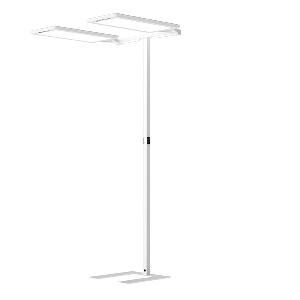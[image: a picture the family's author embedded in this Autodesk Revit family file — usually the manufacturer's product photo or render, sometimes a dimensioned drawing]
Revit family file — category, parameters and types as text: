
# Revit family: yara_doubleu_-_yus_2_15000_vtl_r_ws_cee_s0_c_114268000-00812019_adc4
name_source: partatom
category: Lighting Fixtures
units: mm (PartAtom-declared; Revit-internal decimal feet)

## family parameters
Cut with Voids When Loaded = No
Host = Face
Light Source = No
Part Type = Normal
Room Calculation Point = No
Round Connector Dimension = Use Diameter
Shared = No

## types (1)
- YARA.doubleU - YUS 2/15000/VTL/R/WS/CEE/S0/C (1 x LED, 15000 lm, VTL)
    Apparent Load = 214 VA
    Approval mark = CE
    CIE Flux Codes = 58 87 97 13 100
    Color Rendering = 80-89
    Color Temperature = VTL
    Control Gear = Electronic ballast
    Default Elevation = 1800 mm
    Description = YUS 2/15000/VTL/R/WS/CEE/S0/C|Free-standing luminaire|light source: LED Cold white   |work equipment: Electronic ballast DALI|connected load: 220-240V, 50/60Hz|Power consumption: approx. 210 W|power factor: approx. 0,966|luminous flux: 30000 lm|luminous efficacy: 142 lm/W|light distribution: Direct/indirect|direct ratio: approx. 13 %|color rendering index (CRI): >= 80|chromaticity tolerance:  3 SDCM|technology: Presence and daylight sensor control (PIR)|operation: Wireless switch|luminaire body|material: Aluminium/plastic|surface: Powder coatet|colour: White|lamp cover: Acrylic (PMMA)|tubular section|material: Steel tube|surface: Powder-coated|Form: Tubular section upright|colour of tubular section: White|luminaire base|Form: C-form flat|weight (net): approx. 26.0 kg|mains lead: 3.00 m Mains plug CEE 7/VII|Fastening: Floor standing base|glare control: Conical prismatic screen|luminance(L65): <= 2700 cd/m|unified glare rating(4H 8H): <=  16|special features: App control, Asymmetric radiation, Biodynamic light VTL, Direct and indirect lighting component with edge light and light guidetechnology for a homogeneous light exit, Flicker-free, Magnetic control panel, freely positionable, PIR movement and daylight sensor, TALK Bluetooth|Approval mark: VDE - ENEC|
    Frequency = 50 Hz, 60 Hz
    Height = 24 mm  [stored 0.0787402 ft]
    Lamp = 1 x LED
    Lamp Light Flux = 15000 lm
    Lamp count = 1
    Length = 690 mm
    Luminous efficacy = 140 lm/W
    Manufacturer = Waldmann
    ModVariant = No
    Model = 114268000-00812019
    Mounting Place = Floor
    Mounting Type = Freestanding
    Number of Poles = 1
    OnlyDefault = Yes
    Power Factor = 1
    Product Name = YARA.doubleU - YUS 2/15000/VTL/R/WS/CEE/S0/C
    Product group = Free standing luminaire
    ProductGroupID = 13
    Protection Class = Protection class I
    Protection Degree = IP 20
    RLX_Detail_Level = 1
    RlxData = <blob elided: 67529 chars, md5=bf08c92e>
    Socket = socket
    Standby Power = 0 W
    System Light Flux = 30000 lm
    System Power = 214 W
    Type Comments = Product without accessories
    Type Image = yus-r-ws-c.jpg
    URL = http://relux.com
    VarID = ---
    Voltage = 230 V
    Voltage Range = 220-240 V
    Weight = 0.00 kg
    Width = 358 mm

note: [stored X ft] marks values corroborated as IEEE doubles in the binary element streams (Revit-internal decimal feet)

## geometry (parser evidence)
native form markers: Blend x4, Sweep x21
no freeform markers — native parametric forms only
